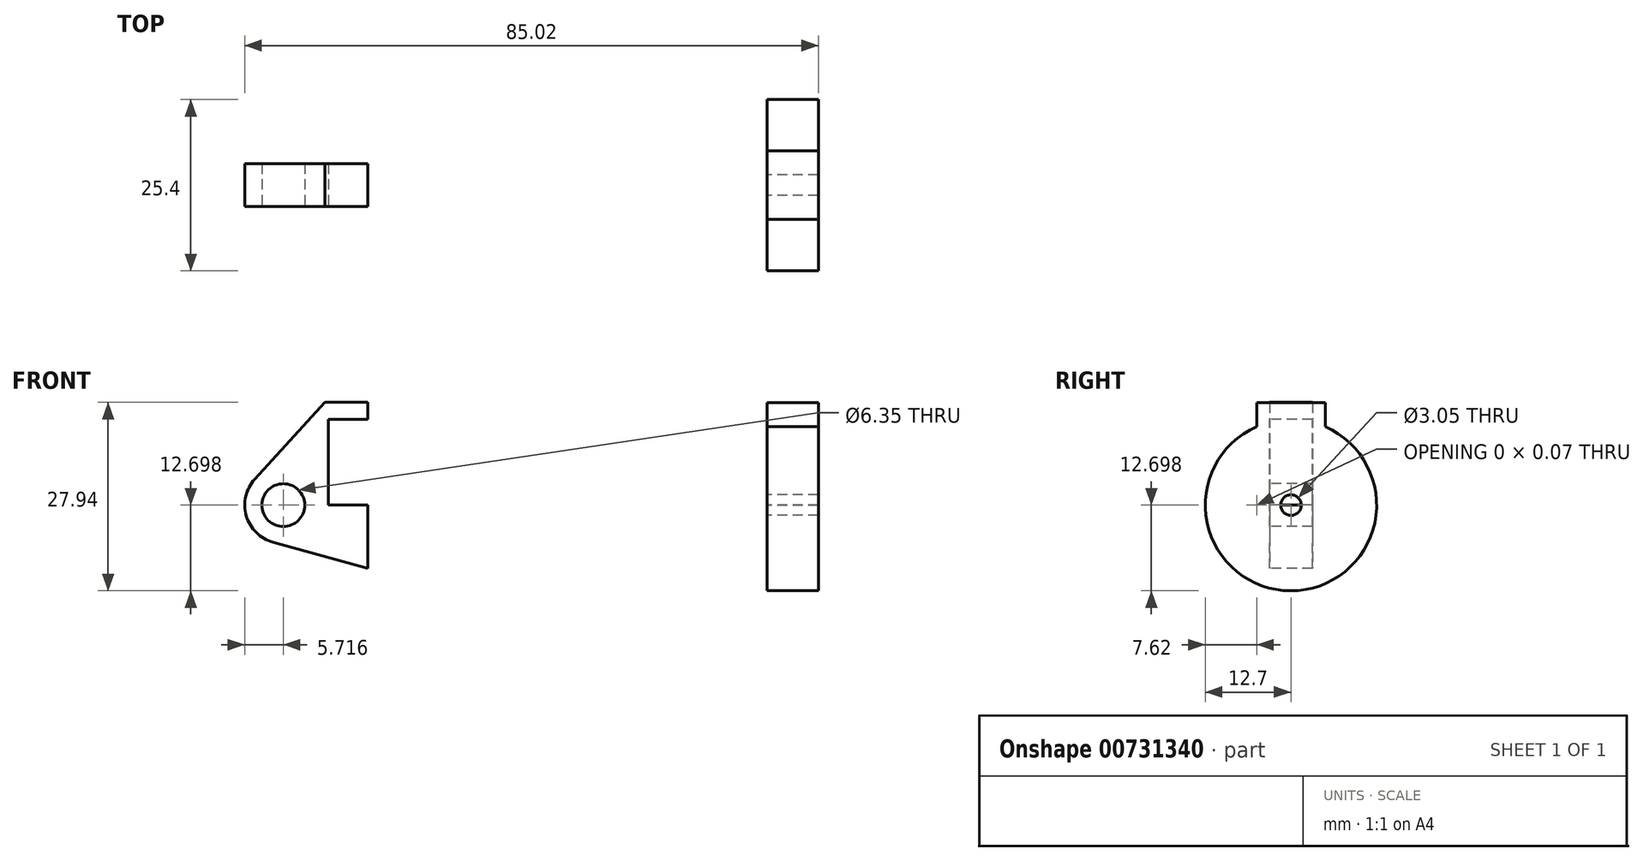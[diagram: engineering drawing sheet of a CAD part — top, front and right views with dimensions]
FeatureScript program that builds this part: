
annotation { "Feature Type Name" : "Feature", "Feature Type Description" : "" }
export const myFeature = defineFeature(function(context is Context, id is Id, definition is map)
    precondition{}
    {
        {
            var Q0;
            Q0=qCreatedBy(makeId("Front.planeOp"),FACE);
            var sketch = newSketch(context, id + "F0", { "sketchPlane" : qUnion([Q0])});
            skLineSegment(sketch, "E0", {"start": v(-16.68, -6.1) * mm, "end": v(-16.68, 6.6) * mm});
            skLineSegment(sketch, "E1", {"start": v(-16.68, 6.6) * mm, "end": v(-6.52, 6.6) * mm});
            skLineSegment(sketch, "E2", {"start": v(-6.52, 6.6) * mm, "end": v(-6.52, 4.07) * mm});
            skLineSegment(sketch, "E3", {"start": v(-6.52, 4.07) * mm, "end": v(39.46, 4.07) * mm});
            skLineSegment(sketch, "E4", {"start": v(39.46, 4.07) * mm, "end": v(39.46, 6.6) * mm});
            skLineSegment(sketch, "E5", {"start": v(39.46, 6.6) * mm, "end": v(49.62, 6.6) * mm});
            skLineSegment(sketch, "E6", {"start": v(49.62, 6.6) * mm, "end": v(49.62, -6.1) * mm});
            skLineSegment(sketch, "E7", {"start": v(49.62, -6.1) * mm, "end": v(-16.68, -6.1) * mm});
            skLineSegment(sketch, "E8", {"start": v(-10.84, 9.15) * mm, "end": v(-17.19, 9.15) * mm});
            skLineSegment(sketch, "E9", {"start": v(-17.19, 9.15) * mm, "end": v(-27.56, -2.24) * mm});
            skLineSegment(sketch, "E10", {"start": v(-16.68, -6.1) * mm, "end": v(-23.33, -6.1) * mm});
            skCircle(sketch, "E11", {"center": v(-23.33, -6.1) * mm, "radius": 5.72 * mm});
            skCircle(sketch, "E12", {"center": v(-23.33, -6.1) * mm, "radius": 3.18 * mm});
            skLineSegment(sketch, "E13", {"start": v(-10.84, 9.15) * mm, "end": v(-10.84, -15.49) * mm});
            skLineSegment(sketch, "E14", {"start": v(-10.84, -15.49) * mm, "end": v(-24.86, -11.6) * mm});
            skSolve(sketch);
        }
        {
            var Q0;
            Q0=sQuery(id+"F0.wireOp",EDGE,"E0");
            var Q1;
            Q1=sQuery(id+"F0.wireOp",EDGE,"E1");
            var Q2;
            Q2=sQuery(id+"F0.wireOp",EDGE,"E2");
            var Q3;
            Q3=sQuery(id+"F0.wireOp",EDGE,"E3");
            var Q4;
            Q4=sQuery(id+"F0.wireOp",EDGE,"E4");
            var Q5;
            Q5=sQuery(id+"F0.wireOp",EDGE,"E5");
            var Q6;
            Q6=sQuery(id+"F0.wireOp",EDGE,"E6");
            var Q7;
            Q7=sQuery(id+"F0.wireOp",EDGE,"E7");
            revolve(context, id + "F1", {"bodyType" : ToolBodyType.SURFACE, "surfaceOperationType" : NewSurfaceOperationType.NEW, "surfaceEntities" : qUnion([Q0, Q1, Q2, Q3, Q4, Q5, Q6]), "axis" : qUnion([Q7]), "revolveType" : RevolveType.FULL});
        }
        {
            var Q0;
            {var subQ0=sQuery(id+"F0.wireOp",EDGE,"E14");Q0=makeQuery(id+"F0.imprint","IMPRINT",FACE,{"disambiguationData":[TD([[makeQuery(id+"F0.imprint","IMPRINT",EDGE,{"derivedFrom":subQ0}),-1.0]])]});}
            var Q1;
            {var subQ5=sQuery(id+"F0.wireOp",EDGE,"E12");Q1=makeQuery(id+"F0.imprint","IMPRINT",FACE,{"disambiguationData":[TD([[makeQuery(id+"F0.imprint","IMPRINT",EDGE,{"derivedFrom":subQ5}),-1.0]])]});}
            var Q2;
            {var subQ1=sQuery(id+"F0.wireOp",EDGE,"E0");Q2=makeQuery(id+"F0.imprint","IMPRINT",FACE,{"disambiguationData":[TD([[makeQuery(id+"F0.imprint","IMPRINT",EDGE,{"derivedFrom":subQ1}),1.0]])]});}
            extrude(context, id + "F2", {"entities" : qUnion([Q0, Q1, Q2]), "endBound" : BoundingType.SYMMETRIC, "oppositeDirection" : true, "depth" : 6.35 * mm, "offsetDistance" : 25.4 * mm});
        }
        {
            var Q0;
            Q0=makeQuery(id+"F1.opRevolve","SWEPT_FACE",FACE,{"disambiguationData":[OSD([sQuery(id+"F0.wireOp",EDGE,"E6")])]});
            var sketch = newSketch(context, id + "F3", { "sketchPlane" : qUnion([Q0])});
            skCircle(sketch, "E15", {"center": v(0, -6.1) * mm, "radius": 1.52 * mm});
            skCircle(sketch, "E16", {"center": v(0, -6.1) * mm, "radius": 5.08 * mm});
            skLineSegment(sketch, "E17.top", {"start": v(-5.08, 9.11) * mm, "end": v(5.08, 9.11) * mm});
            skLineSegment(sketch, "E17.left", {"start": v(-5.08, -6.13) * mm, "end": v(-5.08, 9.11) * mm});
            skLineSegment(sketch, "E17.right", {"start": v(5.08, -6.13) * mm, "end": v(5.08, 9.11) * mm});
            skSolve(sketch);
        }
        {
            var Q0;
            {var subQ0=sQuery(id+"F3.wireOp",EDGE,"E17.left");var subQ1=sQuery(id+"F3.wireOp",EDGE,"E16");var subQ2=makeQuery(id+"F3.imprint","INTERSECT",VERTEX,{"derivedFrom":[subQ1,subQ0]});Q0=makeQuery(id+"F3.imprint","IMPRINT",FACE,{"disambiguationData":[TD([[makeQuery(id+"F3.imprint","IMPRINT",EDGE,{"disambiguationData":[TD([[subQ2,1.0]])],"derivedFrom":subQ1}),-1.0]])]});}
            var Q1;
            {var subQ0=sQuery(id+"F3.wireOp",EDGE,"E17.top");Q1=makeQuery(id+"F3.imprint","IMPRINT",FACE,{"disambiguationData":[TD([[makeQuery(id+"F3.imprint","IMPRINT",EDGE,{"derivedFrom":subQ0}),-1.0]])]});}
            var Q2;
            Q2=makeQuery(id+"F3.imprint","IMPRINT",FACE,{"disambiguationData":[TD([[makeQuery(id+"F3.imprint","IMPRINT",EDGE,{"derivedFrom":sQuery(id+"F3.wireOp",EDGE,"E15")}),-1.0]])]});
            extrude(context, id + "F4", {"entities" : qUnion([Q0, Q1, Q2]), "depth" : 6.35 * mm, "offsetDistance" : 25.4 * mm, "hasSecondDirection" : true, "secondDirectionOppositeDirection" : true, "secondDirectionDepth" : 1.27 * mm});
        }
        {
            var Q0;
            Q0=sQuery(id+"F3.wireOp",EDGE,"E15");
            var Q1;
            Q1=makeQuery(id+"F1.opRevolve","SWEPT_FACE",FACE,{"disambiguationData":[OSD([sQuery(id+"F0.wireOp",EDGE,"E2")])]});
            extrude(context, id + "F5", {"bodyType" : ToolBodyType.SURFACE, "surfaceEntities" : qUnion([Q0]), "endBound" : BoundingType.UP_TO_SURFACE, "oppositeDirection" : true, "depth" : 25.4 * mm, "endBoundEntityFace" : qUnion([Q1]), "offsetDistance" : 25.4 * mm});
        }
    });
